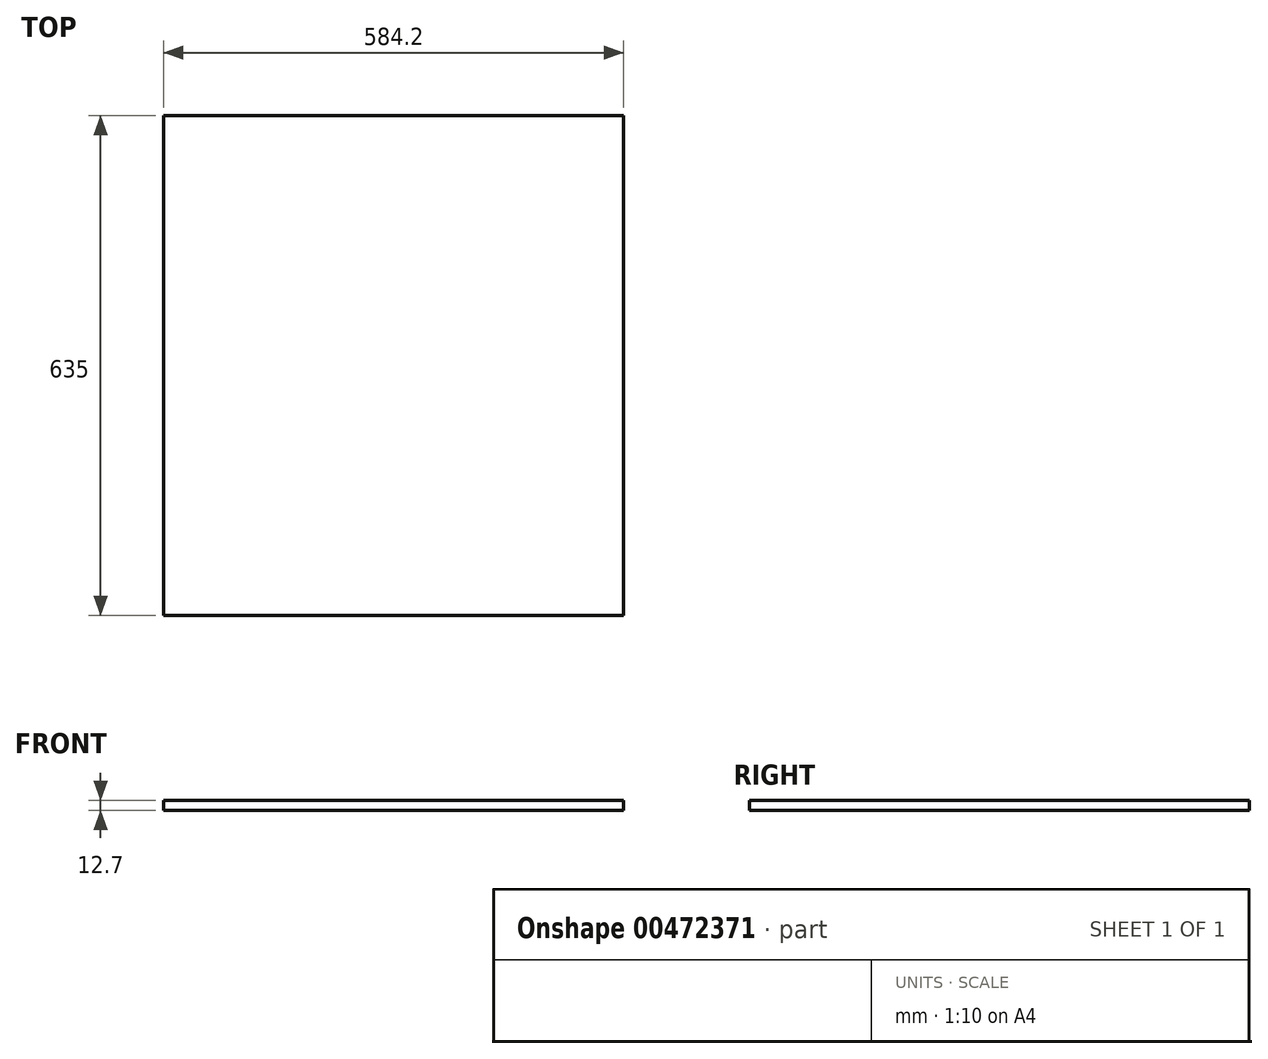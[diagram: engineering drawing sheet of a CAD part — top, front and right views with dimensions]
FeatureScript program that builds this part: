
annotation { "Feature Type Name" : "Feature", "Feature Type Description" : "" }
export const myFeature = defineFeature(function(context is Context, id is Id, definition is map)
    precondition{}
    {
        {
            var Q0;
            Q0=qCreatedBy(makeId("Top.planeOp"),FACE);
            var sketch = newSketch(context, id + "F0", { "sketchPlane" : qUnion([Q0])});
            skLineSegment(sketch, "E0.bottom", {"start": v(-244.93, 376.86) * mm, "end": v(339.27, 376.86) * mm});
            skLineSegment(sketch, "E0.top", {"start": v(-244.93, -258.14) * mm, "end": v(339.27, -258.14) * mm});
            skLineSegment(sketch, "E0.left", {"start": v(-244.93, 376.86) * mm, "end": v(-244.93, -258.14) * mm});
            skLineSegment(sketch, "E0.right", {"start": v(339.27, 376.86) * mm, "end": v(339.27, -258.14) * mm});
            skSolve(sketch);
        }
        {
            var Q0;
            Q0=makeQuery(id+"F0.imprint","IMPRINT",FACE,{"disambiguationData":[TD([[makeQuery(id+"F0.imprint","IMPRINT",EDGE,{"derivedFrom":sQuery(id+"F0.wireOp",EDGE,"E0.bottom")}),-1.0]])]});
            extrude(context, id + "F1", {"entities" : qUnion([Q0]), "depth" : 12.7 * mm});
        }
    });
